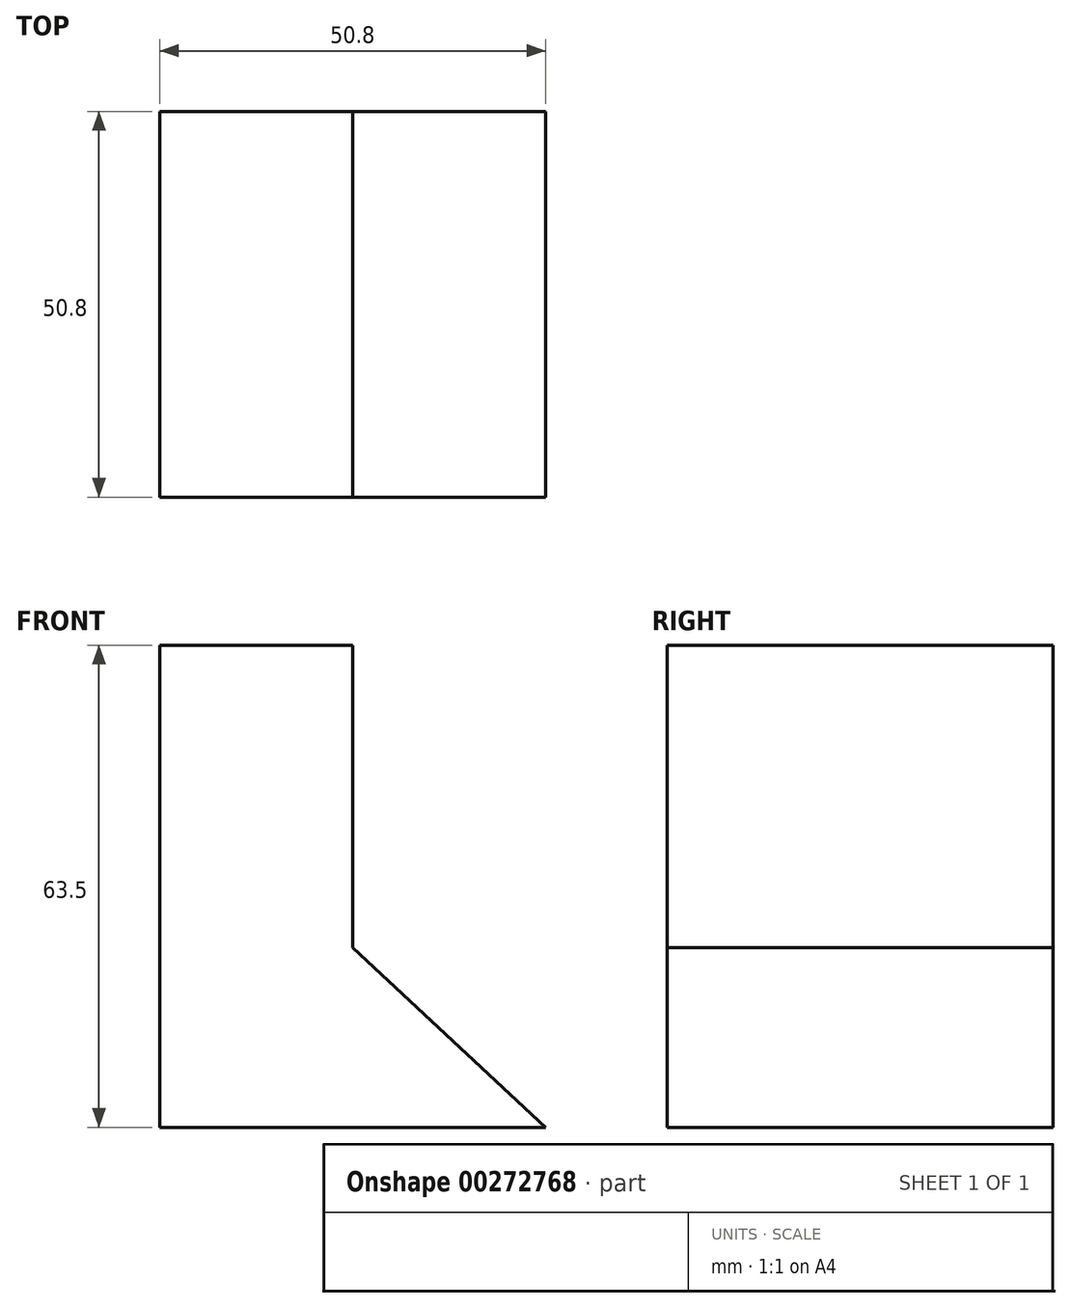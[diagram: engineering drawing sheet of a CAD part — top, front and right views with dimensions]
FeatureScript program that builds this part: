
annotation { "Feature Type Name" : "Feature", "Feature Type Description" : "" }
export const myFeature = defineFeature(function(context is Context, id is Id, definition is map)
    precondition{}
    {
        {
            var Q0;
            Q0=qCreatedBy(makeId("Front.planeOp"),FACE);
            var sketch = newSketch(context, id + "F0", { "sketchPlane" : qUnion([Q0])});
            skLineSegment(sketch, "E0", {"start": v(18.91, -42.65) * mm, "end": v(-31.89, -42.65) * mm});
            skLineSegment(sketch, "E1", {"start": v(-31.89, -42.65) * mm, "end": v(-31.89, 20.85) * mm});
            skLineSegment(sketch, "E2", {"start": v(-31.89, 20.85) * mm, "end": v(-6.49, 20.85) * mm});
            skLineSegment(sketch, "E3", {"start": v(-6.49, 20.85) * mm, "end": v(-6.49, 0) * mm});
            skLineSegment(sketch, "E4", {"start": v(-6.49, 0) * mm, "end": v(-6.49, -18.98) * mm});
            skLineSegment(sketch, "E5", {"start": v(-6.49, -18.98) * mm, "end": v(18.91, -42.65) * mm});
            skSolve(sketch);
        }
        {
            var Q0;
            Q0 = qSketchRegion(id + "F0", true);
            extrude(context, id + "F1", {"entities" : qUnion([Q0]), "depth" : 50.8 * mm});
        }
    });
